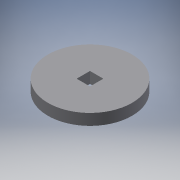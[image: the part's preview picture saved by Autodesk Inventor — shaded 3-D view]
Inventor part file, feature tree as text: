
AUTODESK INVENTOR PART (.ipt)
format: ipt  version: 2017 SP1 (Build 210196100, 196)  size: 147,968 bytes
history: native  units: mm
features: extrude x5, sketch x5, projected_geometry x3, plane x1
ambient origin geometry x8: Origin, YZ Plane, XZ Plane, XY Plane, X Axis, Y Axis, Z Axis, Center Point
bodies: Solid1 (feature_tree)
feature tree (14):
  extrude  "Extrusion1"  Depth=8.0mm TaperAngle=0.0deg
  extrude  "Extrusion2"  Depth=25.0mm
  extrude  "Extrusion3"  Depth=10.0mm
  extrude  "Extrusion4"  Depth=6.0mm TaperAngle=0.0deg
  plane  "Work Plane1"
  extrude  "Extrusion5"  Depth=6.0mm TaperAngle=0.0deg
  sketch  "Sketch1"  dims[d0=60.0mm d2=8.0mm d3=0.0mm]
  sketch  "Sketch2"  dims[d4=6.0mm d5=25.0mm]
  sketch  "Sketch3"  dims[d6=6.0mm d7=0.0mm d8=10.0mm]
  sketch  "Sketch4"  dims[d9=25.0mm d10=6.0mm d11=0.0mm]
  sketch  "Sketch5"  dims[d12=2.8mm d13=6.0mm d14=0.0mm d15=9.525mm d16=6.0mm d17=4.0mm d18=0.0mm]
  projected_geometry  "Projected Loop2"
  projected_geometry  "Projected Loop3"
  projected_geometry  "Projected Loop4"
